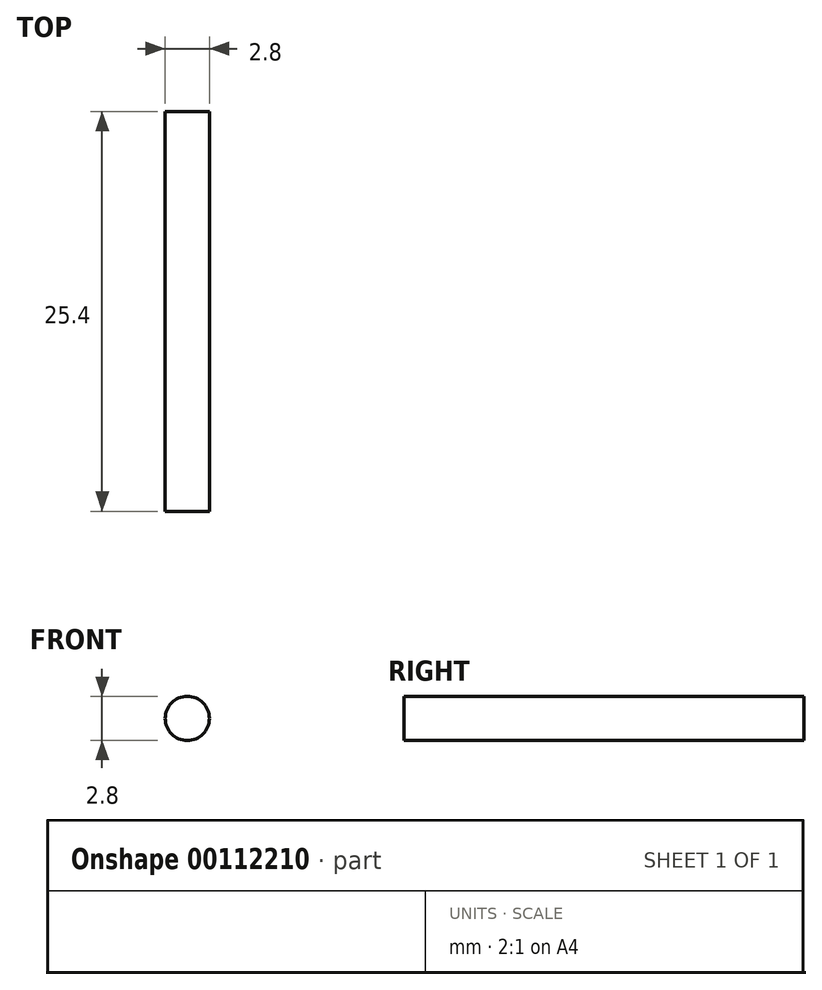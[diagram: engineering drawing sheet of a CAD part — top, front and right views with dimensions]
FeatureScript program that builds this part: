
annotation { "Feature Type Name" : "Feature", "Feature Type Description" : "" }
export const myFeature = defineFeature(function(context is Context, id is Id, definition is map)
    precondition{}
    {
        {
            var Q0;
            Q0=qCreatedBy(makeId("Front.planeOp"),FACE);
            var sketch = newSketch(context, id + "F0", { "sketchPlane" : qUnion([Q0])});
            skCircle(sketch, "E0", {"center": v(0, 0) * mm, "radius": 1.4 * mm});
            skSolve(sketch);
        }
        {
            var Q0;
            Q0=makeQuery(id+"F0.imprint","IMPRINT",FACE,{"disambiguationData":[TD([[makeQuery(id+"F0.imprint","IMPRINT",EDGE,{"derivedFrom":sQuery(id+"F0.wireOp",EDGE,"E0")}),1.0]])]});
            extrude(context, id + "F1", {"entities" : qUnion([Q0]), "endBound" : BoundingType.SYMMETRIC, "depth" : 25.4 * mm});
        }
    });
